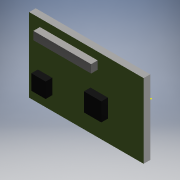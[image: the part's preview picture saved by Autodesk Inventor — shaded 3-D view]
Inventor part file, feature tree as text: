
AUTODESK INVENTOR PART (.ipt)
format: ipt  version: 2019.4 (Build 234330000, 330)  size: 113,664 bytes
history: native  units: mm
features: sketch x3, extrude x2
ambient origin geometry x8: Origin, YZ Plane, XZ Plane, XY Plane, X Axis, Y Axis, Z Axis, Center Point
bodies: Solid1 (feature_tree)
feature tree (5):
  extrude  "Extrusion1"  Depth=5.0mm TaperAngle=0.0deg
  sketch  "Sketch2"
  extrude  "Extrusion2"  [1 undecoded]
  sketch  "Sketch1"  dims[d0=5.0mm d1=0.0mm d2=5.0mm d3=0.0mm]
  sketch  "Sketch3"
note: 1 required parameter value undecoded (feature->parameter linkage not recoverable at this tier; creation-order binding heuristic only, values carry confidence <= 0.55)
